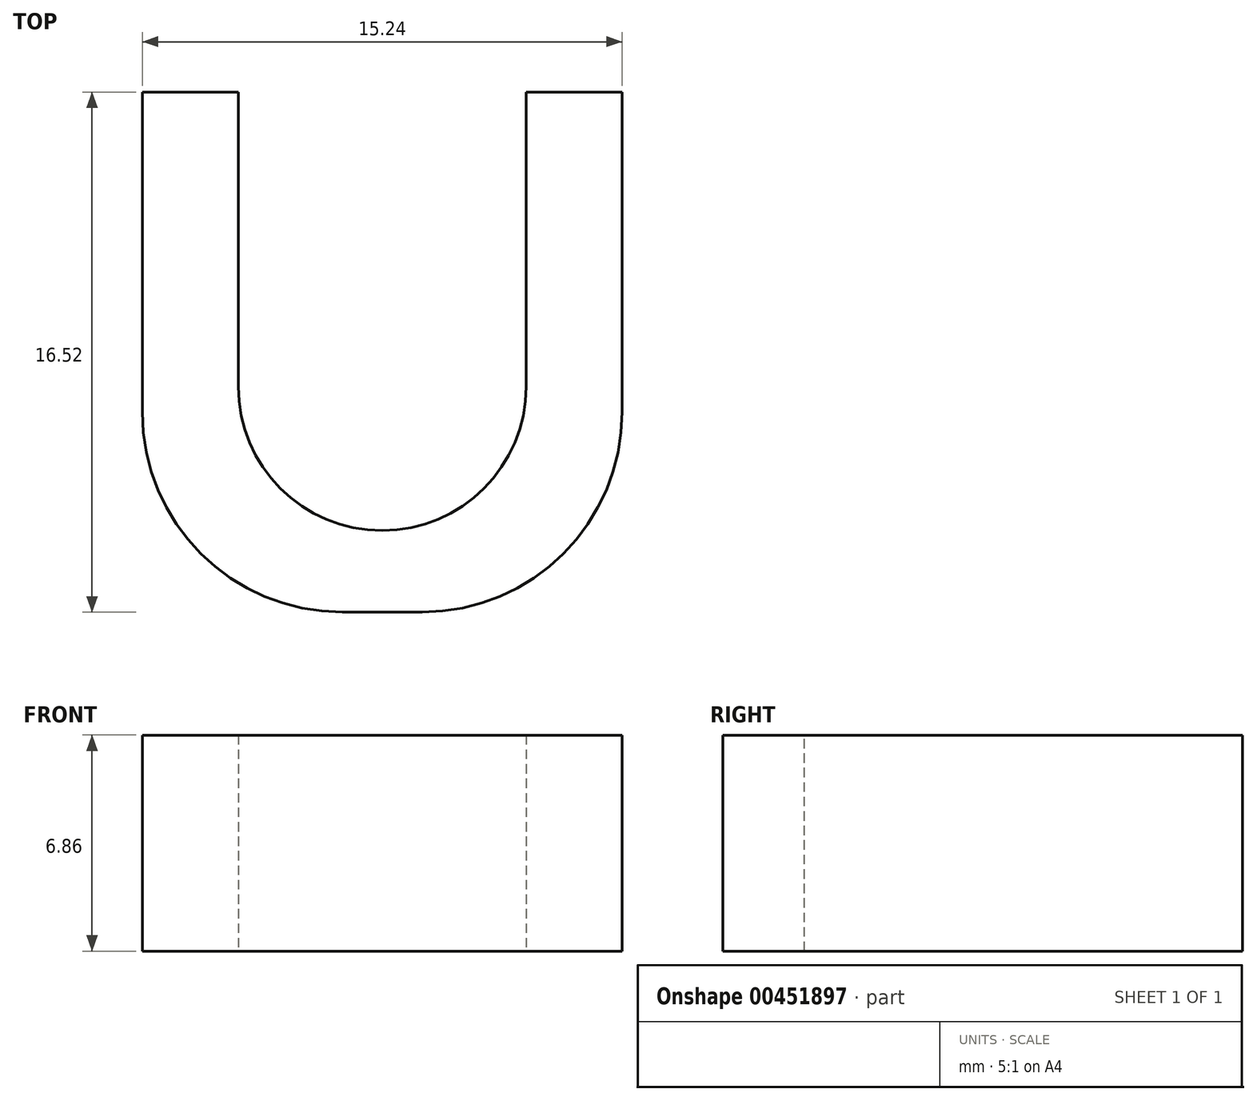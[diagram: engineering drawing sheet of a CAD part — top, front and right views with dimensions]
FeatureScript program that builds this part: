
annotation { "Feature Type Name" : "Feature", "Feature Type Description" : "" }
export const myFeature = defineFeature(function(context is Context, id is Id, definition is map)
    precondition{}
    {
        {
            var Q0;
            Q0=qCreatedBy(makeId("Top.planeOp"),FACE);
            var sketch = newSketch(context, id + "F0", { "sketchPlane" : qUnion([Q0])});
            skLineSegment(sketch, "E0.bottom", {"start": v(7.62, -8.26) * mm, "end": v(-7.62, -8.26) * mm});
            skLineSegment(sketch, "E0.top", {"start": v(7.62, 8.26) * mm, "end": v(-7.62, 8.26) * mm});
            skLineSegment(sketch, "E0.left", {"start": v(7.62, -8.26) * mm, "end": v(7.62, 8.26) * mm});
            skLineSegment(sketch, "E0.right", {"start": v(-7.62, -8.26) * mm, "end": v(-7.62, 8.26) * mm});
            skPoint(sketch, "E0.middle", {"position": v(0, 0) * mm});
            skLineSegment(sketch, "E1.bottom", {"start": v(-4.57, 8.26) * mm, "end": v(4.57, 8.26) * mm});
            skLineSegment(sketch, "E1.top", {"start": v(-4.57, -5.67) * mm, "end": v(4.57, -5.67) * mm});
            skLineSegment(sketch, "E1.left", {"start": v(-4.57, 8.26) * mm, "end": v(-4.57, -5.67) * mm});
            skLineSegment(sketch, "E1.right", {"start": v(4.57, 8.26) * mm, "end": v(4.57, -5.67) * mm});
            skSolve(sketch);
        }
        {
            var Q0;
            Q0=makeQuery(id+"F0.imprint","IMPRINT",FACE,{"disambiguationData":[TD([[makeQuery(id+"F0.imprint","IMPRINT",EDGE,{"derivedFrom":sQuery(id+"F0.wireOp",EDGE,"E0.bottom")}),-1.0]])]});
            extrude(context, id + "F1", {"entities" : qUnion([Q0]), "depth" : 6.86 * mm});
        }
        {
            var Q0;
            Q0=makeQuery(id+"F1.opExtrude","SWEPT_EDGE",EDGE,{"disambiguationData":[OSD([sQuery(id+"F0.wireOp",EDGE,"E1.top"),sQuery(id+"F0.wireOp",EDGE,"E1.left")])]});
            var Q1;
            Q1=makeQuery(id+"F1.opExtrude","SWEPT_EDGE",EDGE,{"disambiguationData":[OSD([sQuery(id+"F0.wireOp",EDGE,"E1.top"),sQuery(id+"F0.wireOp",EDGE,"E1.right")])]});
            fillet(context, id + "F2", {"entities" : qUnion([Q0, Q1]), "radius" : 4.57 * mm, "tangentPropagation" : true, "allowEdgeOverflow" : false});
        }
        {
            var Q0;
            Q0=makeQuery(id+"F1.opExtrude","SWEPT_EDGE",EDGE,{"disambiguationData":[OSD([sQuery(id+"F0.wireOp",EDGE,"E0.bottom"),sQuery(id+"F0.wireOp",EDGE,"E0.left")])]});
            var Q1;
            Q1=makeQuery(id+"F1.opExtrude","SWEPT_EDGE",EDGE,{"disambiguationData":[OSD([sQuery(id+"F0.wireOp",EDGE,"E0.bottom"),sQuery(id+"F0.wireOp",EDGE,"E0.right")])]});
            fillet(context, id + "F3", {"entities" : qUnion([Q0, Q1]), "radius" : 6.35 * mm, "tangentPropagation" : true, "allowEdgeOverflow" : false});
        }
    });
